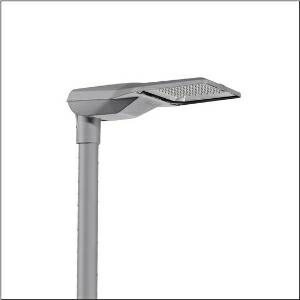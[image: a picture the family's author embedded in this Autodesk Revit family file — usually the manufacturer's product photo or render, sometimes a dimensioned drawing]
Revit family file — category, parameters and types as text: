
# Revit family: streetlight_sl_21_iq_midi___stw1_0a_5xe3e61g08nb_0b2e
name_source: partatom
category: Lighting Fixtures
units: mm (PartAtom-declared; Revit-internal decimal feet)

## family parameters
Cut with Voids When Loaded = No
Host = Face
Light Source = No
Part Type = Normal
Room Calculation Point = No
Round Connector Dimension = Use Diameter
Shared = No

## types (1)
- --- (1 x LED, 20820 lm, 155.5 W, 2700K)
    Apparent Load = 155 VA
    CIE Flux Codes = 39 75 98 100 100
    Color Rendering = 70
    Color Temperature = 2700K
    Default Elevation = 1800 mm
    Description = Streetlight SL 21 iQ midi, mast luminaire, primary light control with lens, of PMMA, primary optical cover: cover, of toughened safety glass, transparent, light distribution: STW1.0a, light emission: direct distribution, primary light characteristic: asymmetric, installation type: post-top, side-entry, LED, High Power LED, rated luminous flux: 20.820lm, luminous efficacy: 134lm/W, light colour: 727, colour temperature: 2700K, control gear: iQ Street-Remote, control: Street-Remote, Auto-Match, Temp-Guard, Lumen-Switch, Night-Set, Smart-Wire, Light-Fading, Desk-Remote (wireless, voltage-free reading and setting of iQ features in the workshop via application-optimized NFC function/RFID function), optimised constant luminous flux control (CLO 2.0), pre-setting: linear dimming characteristic, mains connection: 230..240V, AC, 50/60Hz, start of lifetime: 156W, end of service life: 162W, reduction: 69W, luminaire housing, of diecast aluminium, powder-coated, Siteco® metallic grey (DB 702S), corrosivity category C5 mid according to DIN EN ISO 12944, please order mast flange separately, inclination adjustable: 0°, 5°, 10°, 15°, sealing non-destructively replaceable, multi-level sealing system, length: 644mm, width: 335mm, height: 110mm, mast flange for spigot size: 42mm (side-entry): 5XC10008XM4, 60/48mm (side-entry/post-top): 5XC10108XM2, 76/60mm (side-entry/post-top): 5XC10108XM1, mounting height: 4..8m, protection rating (complete): IP66, insulation class (complete): insulation class II (safety insulation), certification: CE, ENEC, ENEC+, VDE, impact resistance: IK10, permissible operating ambient temperature for outdoor applications: -40..+50°C, standard-compliant lighting for roads and squares, packaging unit: 1 piece

Light Distribution: STW1.0a
    Height = 111 mm
    Lamp = 1 x LED
    Lamp Light Flux = 20820 lm
    Lamp Power = 155.5 W
    Lamp count = 1
    Length = 644 mm
    Luminous efficacy = 134 lm/W
    Manufacturer = Siteco
    ModVariant = No
    Model = 5XE3E61G08NB
    Number of Poles = 1
    OnlyDefault = Yes
    Power Factor = 1
    Product Name = Streetlight SL 21 iQ midi | STW1.0a
    Product group = mast luminaire | pylon top
    ProductGroupID = 6100
    Protection Class = Protection class II
    Protection Degree = IP 66
    RLX_Detail_Level = 1
    RLX_Emergency_Light_Flux = 0 lm
    RLX_Emergency_Type = 0
    RLX_Emergency_Type_DB = No
    RlxData = <blob elided: 27209 chars, md5=c1b643fc>
    Socket = socket
    Standby Power = 0 W
    System Light Flux = 20820 lm
    System Power = 155 W
    Type Comments = factory setting: luminous flux: 100 % | dim-lin: 254 | 823 mA
    Type Image = l_1004298.jpg
    URL = http://relux.com
    VarID = @adj_191189
    Voltage = 0 V
    Weight = 0.00 kg
    Width = 336 mm

## geometry (parser evidence)
native form markers: Blend x4, Sweep x11
no freeform markers — native parametric forms only
